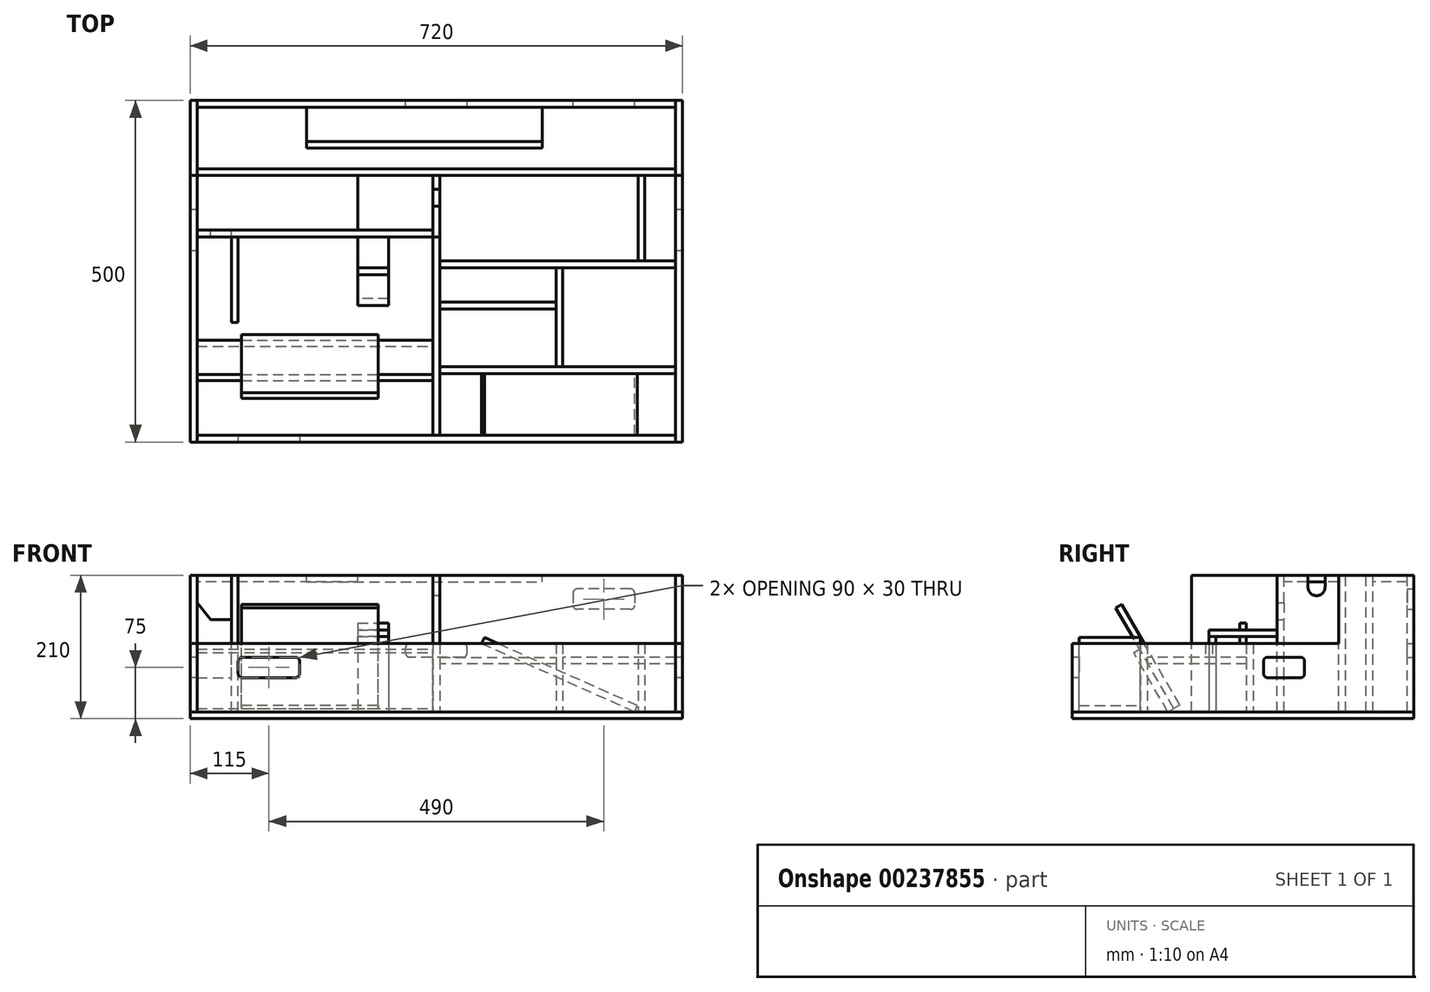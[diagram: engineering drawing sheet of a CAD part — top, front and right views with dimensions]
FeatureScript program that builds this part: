
annotation { "Feature Type Name" : "Feature", "Feature Type Description" : "" }
export const myFeature = defineFeature(function(context is Context, id is Id, definition is map)
    precondition{}
    {
        {
            var Q0;
            Q0=qCreatedBy(makeId("Top.planeOp"),FACE);
            var sketch = newSketch(context, id + "F0", { "sketchPlane" : qUnion([Q0])});
            skLineSegment(sketch, "E0.bottom", {"start": v(360, 250) * mm, "end": v(-360, 250) * mm});
            skLineSegment(sketch, "E0.top", {"start": v(360, -250) * mm, "end": v(-360, -250) * mm});
            skLineSegment(sketch, "E0.left", {"start": v(360, 250) * mm, "end": v(360, -250) * mm});
            skLineSegment(sketch, "E0.right", {"start": v(-360, 250) * mm, "end": v(-360, -250) * mm});
            skPoint(sketch, "E0.middle", {"position": v(0, 0) * mm});
            skSolve(sketch);
        }
        {
            var Q0;
            Q0=makeQuery(id+"F0.imprint","IMPRINT",FACE,{"disambiguationData":[TD([[makeQuery(id+"F0.imprint","IMPRINT",EDGE,{"derivedFrom":sQuery(id+"F0.wireOp",EDGE,"E0.bottom")}),1.0]])]});
            extrude(context, id + "F1", {"entities" : qUnion([Q0]), "depth" : 10 * mm});
        }
        {
            var Q0;
            Q0=makeQuery(id+"F1.opExtrude","SWEPT_FACE",FACE,{"disambiguationData":[OSD([sQuery(id+"F0.wireOp",EDGE,"E0.right")])]});
            var sketch = newSketch(context, id + "F2", { "sketchPlane" : qUnion([Q0])});
            skLineSegment(sketch, "E1.bottom", {"start": v(-250, 10) * mm, "end": v(250, 10) * mm});
            skLineSegment(sketch, "E1.top", {"start": v(-140, 110) * mm, "end": v(250, 110) * mm});
            skLineSegment(sketch, "E1.left", {"start": v(-250, 10) * mm, "end": v(-250, 110) * mm});
            skLineSegment(sketch, "E1.right", {"start": v(250, 10) * mm, "end": v(250, 110) * mm});
            skLineSegment(sketch, "E2.top", {"start": v(-250, 210) * mm, "end": v(-140, 210) * mm});
            skLineSegment(sketch, "E2.left", {"start": v(-250, 110) * mm, "end": v(-250, 210) * mm});
            skLineSegment(sketch, "E2.right", {"start": v(-140, 110) * mm, "end": v(-140, 210) * mm});
            skLineSegment(sketch, "E3.bottom", {"start": v(-250, 10) * mm, "end": v(-90, 10) * mm, "construction": true});
            skLineSegment(sketch, "E3.top", {"start": v(-250, 60) * mm, "end": v(-90, 60) * mm, "construction": true});
            skLineSegment(sketch, "E3.left", {"start": v(-250, 10) * mm, "end": v(-250, 60) * mm, "construction": true});
            skLineSegment(sketch, "E3.right", {"start": v(-90, 10) * mm, "end": v(-90, 60) * mm, "construction": true});
            skLineSegment(sketch, "E4.bottom", {"start": v(-84, 60) * mm, "end": v(-36, 60) * mm});
            skLineSegment(sketch, "E4.top", {"start": v(-84, 90) * mm, "end": v(-36, 90) * mm});
            skLineSegment(sketch, "E4.left", {"start": v(-90, 66) * mm, "end": v(-90, 84) * mm});
            skLineSegment(sketch, "E4.right", {"start": v(-30, 66) * mm, "end": v(-30, 84) * mm});
            skPoint(sketch, "E5.visualSharp", {"position": v(-90, 90) * mm});
            skArc(sketch, "E5.filletArc", {"start": v(-84, 90) * mm, "mid": v(-88.24, 88.24) * mm, "end": v(-90, 84) * mm});
            skPoint(sketch, "E6.visualSharp", {"position": v(-30, 90) * mm});
            skArc(sketch, "E6.filletArc", {"start": v(-30, 84) * mm, "mid": v(-31.76, 88.24) * mm, "end": v(-36, 90) * mm});
            skPoint(sketch, "E7.visualSharp", {"position": v(-30, 60) * mm});
            skArc(sketch, "E7.filletArc", {"start": v(-36, 60) * mm, "mid": v(-31.76, 61.76) * mm, "end": v(-30, 66) * mm});
            skPoint(sketch, "E8.visualSharp", {"position": v(-90, 60) * mm});
            skArc(sketch, "E8.filletArc", {"start": v(-90, 66) * mm, "mid": v(-88.24, 61.76) * mm, "end": v(-84, 60) * mm});
            skSolve(sketch);
        }
        {
            var Q0;
            Q0=makeQuery(id+"F2.imprint","IMPRINT",FACE,{"disambiguationData":[TD([[makeQuery(id+"F2.imprint","IMPRINT",EDGE,{"derivedFrom":sQuery(id+"F2.wireOp",EDGE,"E1.bottom")}),1.0]])]});
            extrude(context, id + "F3", {"entities" : qUnion([Q0]), "oppositeDirection" : true, "depth" : 10 * mm});
        }
        {
            var Q0;
            Q0=makeQuery(id+"F1.opExtrude","SWEPT_FACE",FACE,{"disambiguationData":[OSD([sQuery(id+"F0.wireOp",EDGE,"E0.left")])]});
            var sketch = newSketch(context, id + "F4", { "sketchPlane" : qUnion([Q0])});
            skLineSegment(sketch, "E9.0.0", {"start": v(250, 10) * mm, "end": v(250, 210) * mm});
            skLineSegment(sketch, "E9.0.1", {"start": v(250, 210) * mm, "end": v(140, 210) * mm});
            skLineSegment(sketch, "E9.0.2", {"start": v(140, 210) * mm, "end": v(140, 110) * mm});
            skLineSegment(sketch, "E9.0.3", {"start": v(140, 110) * mm, "end": v(-250, 110) * mm});
            skLineSegment(sketch, "E9.0.4", {"start": v(-250, 110) * mm, "end": v(-250, 10) * mm});
            skLineSegment(sketch, "E9.0.5", {"start": v(-250, 10) * mm, "end": v(250, 10) * mm});
            skLineSegment(sketch, "E10.0", {"start": v(84, 60) * mm, "end": v(36, 60) * mm});
            skLineSegment(sketch, "E11.0", {"start": v(84, 90) * mm, "end": v(36, 90) * mm});
            skArc(sketch, "E12.0", {"start": v(30, 84) * mm, "mid": v(31.76, 88.24) * mm, "end": v(36, 90) * mm});
            skLineSegment(sketch, "E13.0", {"start": v(30, 66) * mm, "end": v(30, 84) * mm});
            skArc(sketch, "E14.0", {"start": v(36, 60) * mm, "mid": v(31.76, 61.76) * mm, "end": v(30, 66) * mm});
            skArc(sketch, "E15.0", {"start": v(90, 66) * mm, "mid": v(88.24, 61.76) * mm, "end": v(84, 60) * mm});
            skLineSegment(sketch, "E16.0", {"start": v(90, 66) * mm, "end": v(90, 84) * mm});
            skArc(sketch, "E17.0", {"start": v(84, 90) * mm, "mid": v(88.24, 88.24) * mm, "end": v(90, 84) * mm});
            skSolve(sketch);
        }
        {
            var Q0;
            Q0 = qSketchRegion(id + "F4", true);
            extrude(context, id + "F5", {"entities" : qUnion([Q0]), "oppositeDirection" : true, "depth" : 10 * mm});
        }
        {
            var Q0;
            Q0=makeQuery(id+"F1.opExtrude","SWEPT_FACE",FACE,{"disambiguationData":[OSD([sQuery(id+"F0.wireOp",EDGE,"E0.top")])]});
            var sketch = newSketch(context, id + "F6", { "sketchPlane" : qUnion([Q0])});
            skLineSegment(sketch, "E18.0", {"start": v(-350, 10) * mm, "end": v(-350, 110) * mm});
            skLineSegment(sketch, "E19.0", {"start": v(350, 110) * mm, "end": v(350, 10) * mm});
            skLineSegment(sketch, "E20", {"start": v(-350, 110) * mm, "end": v(350, 110) * mm});
            skLineSegment(sketch, "E21", {"start": v(-350, 10) * mm, "end": v(350, 10) * mm});
            skLineSegment(sketch, "E22.bottom", {"start": v(-350, 110) * mm, "end": v(-290, 110) * mm, "construction": true});
            skLineSegment(sketch, "E22.top", {"start": v(-350, 90) * mm, "end": v(-290, 90) * mm, "construction": true});
            skLineSegment(sketch, "E22.left", {"start": v(-350, 110) * mm, "end": v(-350, 90) * mm, "construction": true});
            skLineSegment(sketch, "E22.right", {"start": v(-290, 110) * mm, "end": v(-290, 90) * mm, "construction": true});
            skLineSegment(sketch, "E23.bottom", {"start": v(-284, 90) * mm, "end": v(-206, 90) * mm});
            skLineSegment(sketch, "E23.top", {"start": v(-284, 60) * mm, "end": v(-206, 60) * mm});
            skLineSegment(sketch, "E23.left", {"start": v(-290, 84) * mm, "end": v(-290, 66) * mm});
            skLineSegment(sketch, "E23.right", {"start": v(-200, 84) * mm, "end": v(-200, 66) * mm});
            skPoint(sketch, "E24.visualSharp", {"position": v(-200, 90) * mm});
            skArc(sketch, "E24.filletArc", {"start": v(-200, 84) * mm, "mid": v(-201.76, 88.24) * mm, "end": v(-206, 90) * mm});
            skPoint(sketch, "E25.visualSharp", {"position": v(-200, 60) * mm});
            skArc(sketch, "E25.filletArc", {"start": v(-206, 60) * mm, "mid": v(-201.76, 61.76) * mm, "end": v(-200, 66) * mm});
            skPoint(sketch, "E26.visualSharp", {"position": v(-290, 60) * mm});
            skArc(sketch, "E26.filletArc", {"start": v(-290, 66) * mm, "mid": v(-288.24, 61.76) * mm, "end": v(-284, 60) * mm});
            skPoint(sketch, "E27.visualSharp", {"position": v(-290, 90) * mm});
            skArc(sketch, "E27.filletArc", {"start": v(-284, 90) * mm, "mid": v(-288.24, 88.24) * mm, "end": v(-290, 84) * mm});
            skSolve(sketch);
        }
        {
            var Q0;
            Q0 = qSketchRegion(id + "F6", true);
            extrude(context, id + "F7", {"entities" : qUnion([Q0]), "oppositeDirection" : true, "depth" : 10 * mm});
        }
        {
            var Q0;
            Q0=makeQuery(id+"F1.opExtrude","SWEPT_FACE",FACE,{"disambiguationData":[OSD([sQuery(id+"F0.wireOp",EDGE,"E0.bottom")])]});
            var sketch = newSketch(context, id + "F8", { "sketchPlane" : qUnion([Q0])});
            skLineSegment(sketch, "E28.0", {"start": v(-350, 10) * mm, "end": v(-350, 210) * mm});
            skLineSegment(sketch, "E29.0", {"start": v(350, 10) * mm, "end": v(350, 210) * mm});
            skLineSegment(sketch, "E30", {"start": v(-350, 10) * mm, "end": v(350, 10) * mm});
            skLineSegment(sketch, "E31", {"start": v(350, 210) * mm, "end": v(-350, 210) * mm});
            skLineSegment(sketch, "E32.bottom", {"start": v(-350, 210) * mm, "end": v(-290, 210) * mm, "construction": true});
            skLineSegment(sketch, "E32.top", {"start": v(-350, 190) * mm, "end": v(-290, 190) * mm, "construction": true});
            skLineSegment(sketch, "E32.left", {"start": v(-350, 210) * mm, "end": v(-350, 190) * mm, "construction": true});
            skLineSegment(sketch, "E32.right", {"start": v(-290, 210) * mm, "end": v(-290, 190) * mm, "construction": true});
            skLineSegment(sketch, "E33.bottom", {"start": v(-350, 10) * mm, "end": v(-45, 10) * mm, "construction": true});
            skLineSegment(sketch, "E33.top", {"start": v(-350, 90) * mm, "end": v(-45, 90) * mm, "construction": true});
            skLineSegment(sketch, "E33.left", {"start": v(-350, 10) * mm, "end": v(-350, 90) * mm, "construction": true});
            skLineSegment(sketch, "E33.right", {"start": v(-45, 10) * mm, "end": v(-45, 90) * mm, "construction": true});
            skLineSegment(sketch, "E34.bottom", {"start": v(-39, 90) * mm, "end": v(39, 90) * mm});
            skLineSegment(sketch, "E34.top", {"start": v(-39, 110) * mm, "end": v(39, 110) * mm});
            skLineSegment(sketch, "E34.left", {"start": v(-45, 96) * mm, "end": v(-45, 104) * mm});
            skLineSegment(sketch, "E34.right", {"start": v(45, 96) * mm, "end": v(45, 104) * mm});
            skLineSegment(sketch, "E35.bottom", {"start": v(-284, 190) * mm, "end": v(-206, 190) * mm});
            skLineSegment(sketch, "E35.top", {"start": v(-284, 160) * mm, "end": v(-206, 160) * mm});
            skLineSegment(sketch, "E35.left", {"start": v(-290, 184) * mm, "end": v(-290, 166) * mm});
            skLineSegment(sketch, "E35.right", {"start": v(-200, 184) * mm, "end": v(-200, 166) * mm});
            skPoint(sketch, "E36.visualSharp", {"position": v(-290, 190) * mm});
            skArc(sketch, "E36.filletArc", {"start": v(-284, 190) * mm, "mid": v(-288.24, 188.24) * mm, "end": v(-290, 184) * mm});
            skPoint(sketch, "E37.visualSharp", {"position": v(-290, 160) * mm});
            skArc(sketch, "E37.filletArc", {"start": v(-290, 166) * mm, "mid": v(-288.24, 161.76) * mm, "end": v(-284, 160) * mm});
            skPoint(sketch, "E38.visualSharp", {"position": v(-200, 190) * mm});
            skArc(sketch, "E38.filletArc", {"start": v(-200, 184) * mm, "mid": v(-201.76, 188.24) * mm, "end": v(-206, 190) * mm});
            skPoint(sketch, "E39.visualSharp", {"position": v(-200, 160) * mm});
            skArc(sketch, "E39.filletArc", {"start": v(-206, 160) * mm, "mid": v(-201.76, 161.76) * mm, "end": v(-200, 166) * mm});
            skPoint(sketch, "E40.visualSharp", {"position": v(-45, 110) * mm});
            skArc(sketch, "E40.filletArc", {"start": v(-39, 110) * mm, "mid": v(-43.24, 108.24) * mm, "end": v(-45, 104) * mm});
            skPoint(sketch, "E41.visualSharp", {"position": v(45, 110) * mm});
            skArc(sketch, "E41.filletArc", {"start": v(45, 104) * mm, "mid": v(43.24, 108.24) * mm, "end": v(39, 110) * mm});
            skPoint(sketch, "E42.visualSharp", {"position": v(45, 90) * mm});
            skArc(sketch, "E42.filletArc", {"start": v(39, 90) * mm, "mid": v(43.24, 91.76) * mm, "end": v(45, 96) * mm});
            skPoint(sketch, "E43.visualSharp", {"position": v(-45, 90) * mm});
            skArc(sketch, "E43.filletArc", {"start": v(-45, 96) * mm, "mid": v(-43.24, 91.76) * mm, "end": v(-39, 90) * mm});
            skSolve(sketch);
        }
        {
            var Q0;
            Q0=makeQuery(id+"F8.imprint","IMPRINT",FACE,{"disambiguationData":[TD([[makeQuery(id+"F8.imprint","IMPRINT",EDGE,{"derivedFrom":sQuery(id+"F8.wireOp",EDGE,"E28.0")}),-1.0]])]});
            extrude(context, id + "F9", {"entities" : qUnion([Q0]), "oppositeDirection" : true, "depth" : 10 * mm});
        }
        {
            var Q0;
            Q0=makeQuery(id+"F5.opExtrude","SWEPT_FACE",FACE,{"disambiguationData":[OSD([sQuery(id+"F4.wireOp",EDGE,"E9.0.2")])]});
            var sketch = newSketch(context, id + "F10", { "sketchPlane" : qUnion([Q0])});
            skLineSegment(sketch, "E44.0.0", {"start": v(-350, 10) * mm, "end": v(350, 10) * mm});
            skLineSegment(sketch, "E44.0.1", {"start": v(350, 10) * mm, "end": v(350, 210) * mm});
            skLineSegment(sketch, "E44.0.2", {"start": v(350, 210) * mm, "end": v(-350, 210) * mm});
            skLineSegment(sketch, "E44.0.3", {"start": v(-350, 210) * mm, "end": v(-350, 10) * mm});
            skSolve(sketch);
        }
        {
            var Q0;
            {var subQ4=sQuery(id+"F10.wireOp",EDGE,"E44.0.0");Q0=makeQuery(id+"F10.imprint","IMPRINT",FACE,{"disambiguationData":[TD([[makeQuery(id+"F10.imprint","IMPRINT",EDGE,{"derivedFrom":subQ4}),1.0]])]});}
            extrude(context, id + "F11", {"entities" : qUnion([Q0]), "oppositeDirection" : true, "depth" : 10 * mm});
        }
        {
            var Q0;
            Q0=makeQuery(id+"F9.opExtrude","SWEPT_FACE",FACE,{"disambiguationData":[OSD([sQuery(id+"F8.wireOp",EDGE,"E31")])]});
            var sketch = newSketch(context, id + "F12", { "sketchPlane" : qUnion([Q0])});
            skLineSegment(sketch, "E45", {"start": v(-350, 240) * mm, "end": v(-190, 240) * mm, "construction": true});
            skLineSegment(sketch, "E46.bottom", {"start": v(-190, 240) * mm, "end": v(155, 240) * mm});
            skLineSegment(sketch, "E46.top", {"start": v(-190, 190) * mm, "end": v(155, 190) * mm});
            skLineSegment(sketch, "E46.left", {"start": v(-190, 240) * mm, "end": v(-190, 190) * mm});
            skLineSegment(sketch, "E46.right", {"start": v(155, 240) * mm, "end": v(155, 190) * mm});
            skSolve(sketch);
        }
        {
            var Q0;
            Q0=makeQuery(id+"F12.imprint","IMPRINT",FACE,{"disambiguationData":[TD([[makeQuery(id+"F12.imprint","IMPRINT",EDGE,{"derivedFrom":sQuery(id+"F12.wireOp",EDGE,"E46.bottom")}),-1.0]])]});
            extrude(context, id + "F13", {"entities" : qUnion([Q0]), "oppositeDirection" : true, "depth" : 10 * mm});
        }
        {
            var Q0;
            Q0=makeQuery(id+"F13.opExtrude","SWEPT_FACE",FACE,{"disambiguationData":[OSD([sQuery(id+"F12.wireOp",EDGE,"E46.top")])]});
            var sketch = newSketch(context, id + "F14", { "sketchPlane" : qUnion([Q0])});
            skLineSegment(sketch, "E47.0", {"start": v(155, 210) * mm, "end": v(-190, 210) * mm});
            skLineSegment(sketch, "E48.0", {"start": v(155, 10) * mm, "end": v(-190, 10) * mm});
            skLineSegment(sketch, "E49", {"start": v(-190, 210) * mm, "end": v(-190, 10) * mm});
            skPoint(sketch, "E49.endSnap0", {"position": v(-190, 205) * mm});
            skLineSegment(sketch, "E50", {"start": v(155, 210) * mm, "end": v(155, 10) * mm});
            skPoint(sketch, "E51.orphan", {"position": v(-350, 210) * mm});
            skPoint(sketch, "E52.orphan", {"position": v(-360, 10) * mm});
            skPoint(sketch, "E53.orphan", {"position": v(360, 10) * mm});
            skPoint(sketch, "E54.orphan", {"position": v(350, 210) * mm});
            skSolve(sketch);
        }
        {
            var Q0;
            Q0 = qSketchRegion(id + "F14", true);
            extrude(context, id + "F15", {"entities" : qUnion([Q0]), "depth" : 10 * mm});
        }
        {
            var Q0;
            Q0=makeQuery(id+"F11.opExtrude","SWEPT_FACE",FACE,{"disambiguationData":[OSD([sQuery(id+"F10.wireOp",EDGE,"E44.0.2")])]});
            var sketch = newSketch(context, id + "F16", { "sketchPlane" : qUnion([Q0])});
            skLineSegment(sketch, "E55.bottom", {"start": v(-350, 140) * mm, "end": v(-115, 140) * mm});
            skLineSegment(sketch, "E55.top", {"start": v(-350, 60) * mm, "end": v(-115, 60) * mm});
            skLineSegment(sketch, "E55.left", {"start": v(-350, 140) * mm, "end": v(-350, 60) * mm});
            skLineSegment(sketch, "E55.right", {"start": v(-115, 140) * mm, "end": v(-115, 60) * mm});
            skSolve(sketch);
        }
        {
            var Q0;
            Q0 = qSketchRegion(id + "F16", true);
            extrude(context, id + "F17", {"entities" : qUnion([Q0]), "oppositeDirection" : true, "depth" : 10 * mm});
        }
        {
            var Q0;
            Q0=makeQuery(id+"F17.opExtrude","SWEPT_FACE",FACE,{"disambiguationData":[OSD([sQuery(id+"F16.wireOp",EDGE,"E55.top")])]});
            var sketch = newSketch(context, id + "F18", { "sketchPlane" : qUnion([Q0])});
            skLineSegment(sketch, "E56", {"start": v(-350, 210) * mm, "end": v(-5, 210) * mm});
            skLineSegment(sketch, "E57", {"start": v(-5, 210) * mm, "end": v(-5, 10) * mm});
            skLineSegment(sketch, "E58", {"start": v(-5, 10) * mm, "end": v(-350, 10) * mm});
            skLineSegment(sketch, "E59", {"start": v(-350, 10) * mm, "end": v(-350, 60) * mm});
            skLineSegment(sketch, "E60", {"start": v(-350, 60) * mm, "end": v(-300, 60) * mm});
            skLineSegment(sketch, "E61", {"start": v(-300, 60) * mm, "end": v(-300, 145) * mm});
            skLineSegment(sketch, "E62", {"start": v(-300, 145) * mm, "end": v(-330, 145) * mm});
            skLineSegment(sketch, "E63", {"start": v(-350, 210) * mm, "end": v(-350, 170) * mm});
            skLineSegment(sketch, "E64", {"start": v(-350, 170) * mm, "end": v(-330, 145) * mm});
            skSolve(sketch);
        }
        {
            var Q0;
            Q0 = qSketchRegion(id + "F18", true);
            extrude(context, id + "F19", {"entities" : qUnion([Q0]), "depth" : 10 * mm});
        }
        {
            var Q0;
            Q0=makeQuery(id+"F19.opExtrude","SWEPT_FACE",FACE,{"disambiguationData":[OSD([sQuery(id+"F18.wireOp",EDGE,"E57")])]});
            var sketch = newSketch(context, id + "F20", { "sketchPlane" : qUnion([Q0])});
            skLineSegment(sketch, "E65.0", {"start": v(50, 210) * mm, "end": v(50, 110) * mm});
            skLineSegment(sketch, "E66.0", {"start": v(140, 210) * mm, "end": v(140, 110) * mm});
            skLineSegment(sketch, "E66.1", {"start": v(140, 210) * mm, "end": v(140, 10) * mm});
            skLineSegment(sketch, "E67.0", {"start": v(140, 210) * mm, "end": v(120, 210) * mm});
            skLineSegment(sketch, "E67.1", {"start": v(50, 210) * mm, "end": v(60, 210) * mm});
            skLineSegment(sketch, "E68", {"start": v(50, 10) * mm, "end": v(140, 10) * mm});
            skLineSegment(sketch, "E69", {"start": v(140, 210) * mm, "end": v(120, 210) * mm, "construction": true});
            skLineSegment(sketch, "E70", {"start": v(107.5, 210) * mm, "end": v(107.5, 192.5) * mm, "construction": true});
            skArc(sketch, "E71", {"start": v(95, 192.5) * mm, "mid": v(107.5, 180) * mm, "end": v(120, 192.5) * mm});
            skLineSegment(sketch, "E72", {"start": v(120, 210) * mm, "end": v(120, 192.5) * mm});
            skLineSegment(sketch, "E73", {"start": v(95, 192.5) * mm, "end": v(95, 210) * mm});
            skLineSegment(sketch, "E74.trimOffspring", {"start": v(95, 210) * mm, "end": v(60, 210) * mm});
            skLineSegment(sketch, "E75.0", {"start": v(-240, 110) * mm, "end": v(-240, 10) * mm});
            skLineSegment(sketch, "E76", {"start": v(50, 10) * mm, "end": v(-240, 10) * mm});
            skLineSegment(sketch, "E77", {"start": v(-240, 110) * mm, "end": v(50, 110) * mm});
            skSolve(sketch);
        }
        {
            var Q0;
            Q0 = qSketchRegion(id + "F20", true);
            extrude(context, id + "F21", {"entities" : qUnion([Q0]), "depth" : 10 * mm});
        }
        {
            var Q0;
            Q0=makeQuery(id+"F21.opExtrude","CAP_FACE",FACE,{"disambiguationData":[OSD([sQuery(id+"F20.wireOp",EDGE,"E65.0"),sQuery(id+"F20.wireOp",EDGE,"E66.1"),sQuery(id+"F20.wireOp",EDGE,"E67.0"),sQuery(id+"F20.wireOp",EDGE,"E67.1"),sQuery(id+"F20.wireOp",EDGE,"E68"),sQuery(id+"F20.wireOp",EDGE,"E71"),sQuery(id+"F20.wireOp",EDGE,"E72"),sQuery(id+"F20.wireOp",EDGE,"E73"),sQuery(id+"F20.wireOp",EDGE,"E74.trimOffspring"),sQuery(id+"F20.wireOp",EDGE,"E75.0"),sQuery(id+"F20.wireOp",EDGE,"E76"),sQuery(id+"F20.wireOp",EDGE,"E77")])],"isStart":false});
            var sketch = newSketch(context, id + "F22", { "sketchPlane" : qUnion([Q0])});
            skLineSegment(sketch, "E78", {"start": v(140, 110) * mm, "end": v(15, 110) * mm, "construction": true});
            skLineSegment(sketch, "E79", {"start": v(15, 110) * mm, "end": v(-140, 110) * mm, "construction": true});
            skLineSegment(sketch, "E80.bottom", {"start": v(15, 110) * mm, "end": v(5, 110) * mm});
            skLineSegment(sketch, "E80.top", {"start": v(15, 10) * mm, "end": v(5, 10) * mm});
            skLineSegment(sketch, "E80.left", {"start": v(15, 110) * mm, "end": v(15, 10) * mm});
            skLineSegment(sketch, "E80.right", {"start": v(5, 110) * mm, "end": v(5, 10) * mm});
            skLineSegment(sketch, "E81.bottom", {"start": v(-140, 110) * mm, "end": v(-150, 110) * mm});
            skLineSegment(sketch, "E81.top", {"start": v(-140, 10) * mm, "end": v(-150, 10) * mm});
            skLineSegment(sketch, "E81.left", {"start": v(-140, 110) * mm, "end": v(-140, 10) * mm});
            skLineSegment(sketch, "E81.right", {"start": v(-150, 110) * mm, "end": v(-150, 10) * mm});
            skSolve(sketch);
        }
        {
            var Q0;
            Q0 = qSketchRegion(id + "F22", true);
            extrude(context, id + "F23", {"entities" : qUnion([Q0]), "endBound" : BoundingType.UP_TO_NEXT, "depth" : 25 * mm});
        }
        {
            var Q0;
            Q0=makeQuery(id+"F11.opExtrude","CAP_FACE",FACE,{"disambiguationData":[OSD([sQuery(id+"F10.wireOp",EDGE,"E44.0.0"),sQuery(id+"F10.wireOp",EDGE,"E44.0.1"),sQuery(id+"F10.wireOp",EDGE,"E44.0.2"),sQuery(id+"F10.wireOp",EDGE,"E44.0.3")])],"isStart":true});
            var sketch = newSketch(context, id + "F24", { "sketchPlane" : qUnion([Q0])});
            skLineSegment(sketch, "E82", {"start": v(350, 10) * mm, "end": v(305, 10) * mm, "construction": true});
            skLineSegment(sketch, "E83.bottom", {"start": v(305, 10) * mm, "end": v(295, 10) * mm});
            skLineSegment(sketch, "E83.top", {"start": v(305, 110) * mm, "end": v(295, 110) * mm});
            skLineSegment(sketch, "E83.left", {"start": v(305, 10) * mm, "end": v(305, 110) * mm});
            skLineSegment(sketch, "E83.right", {"start": v(295, 10) * mm, "end": v(295, 110) * mm});
            skSolve(sketch);
        }
        {
            var Q0;
            Q0 = qSketchRegion(id + "F24", true);
            extrude(context, id + "F25", {"entities" : qUnion([Q0]), "endBound" : BoundingType.UP_TO_NEXT, "depth" : 25 * mm});
        }
        {
            var Q0;
            Q0=makeQuery(id+"F21.opExtrude","CAP_FACE",FACE,{"disambiguationData":[OSD([sQuery(id+"F20.wireOp",EDGE,"E65.0"),sQuery(id+"F20.wireOp",EDGE,"E66.1"),sQuery(id+"F20.wireOp",EDGE,"E67.0"),sQuery(id+"F20.wireOp",EDGE,"E67.1"),sQuery(id+"F20.wireOp",EDGE,"E68"),sQuery(id+"F20.wireOp",EDGE,"E71"),sQuery(id+"F20.wireOp",EDGE,"E72"),sQuery(id+"F20.wireOp",EDGE,"E73"),sQuery(id+"F20.wireOp",EDGE,"E74.trimOffspring"),sQuery(id+"F20.wireOp",EDGE,"E75.0"),sQuery(id+"F20.wireOp",EDGE,"E76"),sQuery(id+"F20.wireOp",EDGE,"E77")])],"isStart":false});
            var sketch = newSketch(context, id + "F26", { "sketchPlane" : qUnion([Q0])});
            skLineSegment(sketch, "E84.0", {"start": v(5, 90) * mm, "end": v(5, 80) * mm});
            skPoint(sketch, "E85.orphan", {"position": v(5, 10) * mm});
            skLineSegment(sketch, "E86.bottom", {"start": v(5, 80) * mm, "end": v(-140, 80) * mm});
            skLineSegment(sketch, "E86.top", {"start": v(5, 90) * mm, "end": v(-140, 90) * mm});
            skLineSegment(sketch, "E86.left", {"start": v(5, 80) * mm, "end": v(5, 90) * mm});
            skLineSegment(sketch, "E86.right", {"start": v(-140, 80) * mm, "end": v(-140, 90) * mm});
            skPoint(sketch, "E87.orphan", {"position": v(5, 110) * mm});
            skSolve(sketch);
        }
        {
            var Q0;
            Q0 = qSketchRegion(id + "F26", true);
            extrude(context, id + "F27", {"entities" : qUnion([Q0]), "depth" : 170 * mm});
        }
        {
            var Q0;
            Q0=makeQuery(id+"F27.opExtrude","CAP_FACE",FACE,{"disambiguationData":[OSD([sQuery(id+"F26.wireOp",EDGE,"E86.bottom"),sQuery(id+"F26.wireOp",EDGE,"E86.top"),sQuery(id+"F26.wireOp",EDGE,"E86.left"),sQuery(id+"F26.wireOp",EDGE,"E86.right")])],"isStart":false});
            var sketch = newSketch(context, id + "F28", { "sketchPlane" : qUnion([Q0])});
            skLineSegment(sketch, "E88.0", {"start": v(-140, 110) * mm, "end": v(-140, 10) * mm});
            skLineSegment(sketch, "E89.0", {"start": v(5, 110) * mm, "end": v(5, 10) * mm});
            skLineSegment(sketch, "E90", {"start": v(-140, 110) * mm, "end": v(5, 110) * mm});
            skLineSegment(sketch, "E91", {"start": v(5, 10) * mm, "end": v(-140, 10) * mm});
            skSolve(sketch);
        }
        {
            var Q0;
            Q0 = qSketchRegion(id + "F28", true);
            extrude(context, id + "F29", {"entities" : qUnion([Q0]), "depth" : 10 * mm});
        }
        {
            var Q0;
            Q0=makeQuery(id+"F27.opExtrude","SWEPT_FACE",FACE,{"disambiguationData":[OSD([sQuery(id+"F26.wireOp",EDGE,"E86.top")])]});
            var sketch = newSketch(context, id + "F30", { "sketchPlane" : qUnion([Q0])});
            skLineSegment(sketch, "E92", {"start": v(5, -140) * mm, "end": v(5, -55) * mm, "construction": true});
            skLineSegment(sketch, "E93.bottom", {"start": v(5, -55) * mm, "end": v(175, -55) * mm});
            skLineSegment(sketch, "E93.top", {"start": v(5, -45) * mm, "end": v(175, -45) * mm});
            skLineSegment(sketch, "E93.left", {"start": v(5, -55) * mm, "end": v(5, -45) * mm});
            skLineSegment(sketch, "E93.right", {"start": v(175, -55) * mm, "end": v(175, -45) * mm});
            skSolve(sketch);
        }
        {
            var Q0;
            Q0 = qSketchRegion(id + "F30", true);
            var Q1;
            Q1=makeQuery(id+"F21.opExtrude","SWEPT_FACE",FACE,{"disambiguationData":[OSD([sQuery(id+"F20.wireOp",EDGE,"E77")])]});
            extrude(context, id + "F31", {"entities" : qUnion([Q0]), "endBound" : BoundingType.UP_TO_SURFACE, "endBoundEntityFace" : qUnion([Q1]), "depth" : 25 * mm});
        }
        {
            var Q0;
            Q0=makeQuery(id+"F29.opExtrude","CAP_FACE",FACE,{"disambiguationData":[OSD([sQuery(id+"F28.wireOp",EDGE,"E88.0"),sQuery(id+"F28.wireOp",EDGE,"E89.0"),sQuery(id+"F28.wireOp",EDGE,"E90"),sQuery(id+"F28.wireOp",EDGE,"E91")])],"isStart":false});
            var sketch = newSketch(context, id + "F32", { "sketchPlane" : qUnion([Q0])});
            skLineSegment(sketch, "E94.0", {"start": v(5, 90) * mm, "end": v(-140, 90) * mm});
            skLineSegment(sketch, "E95.0", {"start": v(5, 80) * mm, "end": v(-140, 80) * mm});
            skLineSegment(sketch, "E96", {"start": v(-140, 90) * mm, "end": v(-140, 80) * mm});
            skLineSegment(sketch, "E97", {"start": v(5, 90) * mm, "end": v(5, 80) * mm});
            skSolve(sketch);
        }
        {
            var Q0;
            Q0 = qSketchRegion(id + "F32", true);
            extrude(context, id + "F33", {"entities" : qUnion([Q0]), "endBound" : BoundingType.UP_TO_NEXT, "depth" : 25 * mm});
        }
        {
            var Q0;
            Q0=makeQuery(id+"F19.opExtrude","CAP_FACE",FACE,{"disambiguationData":[OSD([sQuery(id+"F18.wireOp",EDGE,"E56"),sQuery(id+"F18.wireOp",EDGE,"E57"),sQuery(id+"F18.wireOp",EDGE,"E58"),sQuery(id+"F18.wireOp",EDGE,"E59"),sQuery(id+"F18.wireOp",EDGE,"E60"),sQuery(id+"F18.wireOp",EDGE,"E61"),sQuery(id+"F18.wireOp",EDGE,"E62"),sQuery(id+"F18.wireOp",EDGE,"E63"),sQuery(id+"F18.wireOp",EDGE,"E64")])],"isStart":false});
            var sketch = newSketch(context, id + "F34", { "sketchPlane" : qUnion([Q0])});
            skLineSegment(sketch, "E98.0", {"start": v(-300, 60) * mm, "end": v(-300, 145) * mm});
            skLineSegment(sketch, "E99", {"start": v(-300, 60) * mm, "end": v(-300, 10) * mm});
            skLineSegment(sketch, "E100", {"start": v(-300, 10) * mm, "end": v(-290, 10) * mm});
            skLineSegment(sketch, "E101", {"start": v(-290, 10) * mm, "end": v(-290, 210) * mm});
            skLineSegment(sketch, "E102", {"start": v(-290, 210) * mm, "end": v(-300, 210) * mm});
            skLineSegment(sketch, "E103", {"start": v(-300, 210) * mm, "end": v(-300, 145) * mm});
            skSolve(sketch);
        }
        {
            var Q0;
            Q0 = qSketchRegion(id + "F34", true);
            extrude(context, id + "F35", {"entities" : qUnion([Q0]), "depth" : 125 * mm});
        }
        {
            var Q0;
            Q0=makeQuery(id+"F19.opExtrude","CAP_FACE",FACE,{"disambiguationData":[OSD([sQuery(id+"F18.wireOp",EDGE,"E56"),sQuery(id+"F18.wireOp",EDGE,"E57"),sQuery(id+"F18.wireOp",EDGE,"E58"),sQuery(id+"F18.wireOp",EDGE,"E59"),sQuery(id+"F18.wireOp",EDGE,"E60"),sQuery(id+"F18.wireOp",EDGE,"E61"),sQuery(id+"F18.wireOp",EDGE,"E62"),sQuery(id+"F18.wireOp",EDGE,"E63"),sQuery(id+"F18.wireOp",EDGE,"E64")])],"isStart":false});
            var sketch = newSketch(context, id + "F36", { "sketchPlane" : qUnion([Q0])});
            skLineSegment(sketch, "E104.bottom", {"start": v(-5, 210) * mm, "end": v(-70, 210) * mm, "construction": true});
            skLineSegment(sketch, "E104.top", {"start": v(-5, 130) * mm, "end": v(-70, 130) * mm, "construction": true});
            skLineSegment(sketch, "E104.left", {"start": v(-5, 210) * mm, "end": v(-5, 130) * mm, "construction": true});
            skLineSegment(sketch, "E104.right", {"start": v(-70, 210) * mm, "end": v(-70, 130) * mm, "construction": true});
            skLineSegment(sketch, "E105.bottom", {"start": v(-70, 130) * mm, "end": v(-115, 130) * mm});
            skLineSegment(sketch, "E105.top", {"start": v(-70, 120) * mm, "end": v(-115, 120) * mm});
            skLineSegment(sketch, "E105.left", {"start": v(-70, 130) * mm, "end": v(-70, 120) * mm});
            skLineSegment(sketch, "E105.right", {"start": v(-115, 130) * mm, "end": v(-115, 120) * mm});
            skSolve(sketch);
        }
        {
            var Q0;
            Q0 = qSketchRegion(id + "F36", true);
            extrude(context, id + "F37", {"entities" : qUnion([Q0]), "depth" : 100 * mm});
        }
        {
            var Q0;
            Q0=makeQuery(id+"F37.opExtrude","CAP_FACE",FACE,{"disambiguationData":[OSD([sQuery(id+"F36.wireOp",EDGE,"E105.bottom"),sQuery(id+"F36.wireOp",EDGE,"E105.top"),sQuery(id+"F36.wireOp",EDGE,"E105.left"),sQuery(id+"F36.wireOp",EDGE,"E105.right")])],"isStart":false});
            var sketch = newSketch(context, id + "F38", { "sketchPlane" : qUnion([Q0])});
            skLineSegment(sketch, "E106.bottom", {"start": v(-115, 120) * mm, "end": v(-70, 120) * mm});
            skLineSegment(sketch, "E106.top", {"start": v(-115, 10) * mm, "end": v(-70, 10) * mm});
            skLineSegment(sketch, "E106.left", {"start": v(-115, 120) * mm, "end": v(-115, 10) * mm});
            skLineSegment(sketch, "E106.right", {"start": v(-70, 120) * mm, "end": v(-70, 10) * mm});
            skSolve(sketch);
        }
        {
            var Q0;
            Q0 = qSketchRegion(id + "F38", true);
            extrude(context, id + "F39", {"entities" : qUnion([Q0]), "oppositeDirection" : true, "depth" : 10 * mm});
        }
        {
            var Q0;
            Q0=makeQuery(id+"F37.opExtrude","SWEPT_FACE",FACE,{"disambiguationData":[OSD([sQuery(id+"F36.wireOp",EDGE,"E105.bottom")])]});
            var sketch = newSketch(context, id + "F40", { "sketchPlane" : qUnion([Q0])});
            skLineSegment(sketch, "E107", {"start": v(-115, -50) * mm, "end": v(-115, -5) * mm, "construction": true});
            skLineSegment(sketch, "E108.bottom", {"start": v(-115, -5) * mm, "end": v(-70, -5) * mm});
            skLineSegment(sketch, "E108.top", {"start": v(-115, 5) * mm, "end": v(-70, 5) * mm});
            skLineSegment(sketch, "E108.left", {"start": v(-115, -5) * mm, "end": v(-115, 5) * mm});
            skLineSegment(sketch, "E108.right", {"start": v(-70, -5) * mm, "end": v(-70, 5) * mm});
            skSolve(sketch);
        }
        {
            var Q0;
            Q0=makeQuery(id+"F40.imprint","IMPRINT",FACE,{"disambiguationData":[TD([[makeQuery(id+"F40.imprint","IMPRINT",EDGE,{"derivedFrom":sQuery(id+"F40.wireOp",EDGE,"E108.bottom")}),1.0]])]});
            extrude(context, id + "F41", {"entities" : qUnion([Q0]), "depth" : 10 * mm});
        }
        {
            var Q0;
            Q0=makeQuery(id+"F40.imprint","IMPRINT",FACE,{"disambiguationData":[TD([[makeQuery(id+"F40.imprint","IMPRINT",EDGE,{"derivedFrom":sQuery(id+"F40.wireOp",EDGE,"E108.bottom")}),1.0]])]});
            extrude(context, id + "F42", {"entities" : qUnion([Q0]), "oppositeDirection" : true, "depth" : 20 * mm, "hasSecondDirection" : true, "secondDirectionOppositeDirection" : true, "secondDirectionDepth" : 10 * mm});
        }
        {
            var Q0;
            Q0=makeQuery(id+"F23.opExtrude","SWEPT_FACE",FACE,{"disambiguationData":[OSD([sQuery(id+"F22.wireOp",EDGE,"E81.right")])]});
            var sketch = newSketch(context, id + "F43", { "sketchPlane" : qUnion([Q0])});
            skLineSegment(sketch, "E109", {"start": v(350, 10) * mm, "end": v(290, 10) * mm, "construction": true});
            skLineSegment(sketch, "E110", {"start": v(290, 10) * mm, "end": v(66.18, 109.65) * mm});
            skLineSegment(sketch, "E111", {"start": v(66.18, 109.65) * mm, "end": v(70.25, 118.79) * mm});
            skLineSegment(sketch, "E112", {"start": v(290, 10) * mm, "end": v(294.07, 19.14) * mm});
            skLineSegment(sketch, "E113", {"start": v(294.07, 19.14) * mm, "end": v(70.25, 118.79) * mm});
            skSolve(sketch);
        }
        {
            var Q0;
            Q0 = qSketchRegion(id + "F43", true);
            var Q1;
            Q1=makeQuery(id+"F7.opExtrude","CAP_FACE",FACE,{"disambiguationData":[OSD([sQuery(id+"F6.wireOp",EDGE,"E18.0"),sQuery(id+"F6.wireOp",EDGE,"E19.0"),sQuery(id+"F6.wireOp",EDGE,"E20"),sQuery(id+"F6.wireOp",EDGE,"E21"),sQuery(id+"F6.wireOp",EDGE,"E23.bottom"),sQuery(id+"F6.wireOp",EDGE,"E23.top"),sQuery(id+"F6.wireOp",EDGE,"E23.left"),sQuery(id+"F6.wireOp",EDGE,"E23.right"),sQuery(id+"F6.wireOp",EDGE,"E24.filletArc"),sQuery(id+"F6.wireOp",EDGE,"E25.filletArc"),sQuery(id+"F6.wireOp",EDGE,"E26.filletArc"),sQuery(id+"F6.wireOp",EDGE,"E27.filletArc")])],"isStart":false});
            extrude(context, id + "F44", {"entities" : qUnion([Q0]), "endBound" : BoundingType.UP_TO_SURFACE, "endBoundEntityFace" : qUnion([Q1]), "depth" : 25 * mm});
        }
        {
            var Q0;
            Q0=makeQuery(id+"F21.opExtrude","CAP_FACE",FACE,{"disambiguationData":[OSD([sQuery(id+"F20.wireOp",EDGE,"E65.0"),sQuery(id+"F20.wireOp",EDGE,"E66.1"),sQuery(id+"F20.wireOp",EDGE,"E67.0"),sQuery(id+"F20.wireOp",EDGE,"E67.1"),sQuery(id+"F20.wireOp",EDGE,"E68"),sQuery(id+"F20.wireOp",EDGE,"E71"),sQuery(id+"F20.wireOp",EDGE,"E72"),sQuery(id+"F20.wireOp",EDGE,"E73"),sQuery(id+"F20.wireOp",EDGE,"E74.trimOffspring"),sQuery(id+"F20.wireOp",EDGE,"E75.0"),sQuery(id+"F20.wireOp",EDGE,"E76"),sQuery(id+"F20.wireOp",EDGE,"E77")])],"isStart":true});
            var sketch = newSketch(context, id + "F45", { "sketchPlane" : qUnion([Q0])});
            skLineSegment(sketch, "E114", {"start": v(240, 10) * mm, "end": v(110, 10) * mm, "construction": true});
            skLineSegment(sketch, "E115", {"start": v(110, 10) * mm, "end": v(160, 96.6) * mm});
            skLineSegment(sketch, "E116", {"start": v(160, 96.6) * mm, "end": v(151.34, 101.6) * mm});
            skLineSegment(sketch, "E117", {"start": v(110, 10) * mm, "end": v(101.34, 15) * mm});
            skLineSegment(sketch, "E118", {"start": v(101.34, 15) * mm, "end": v(151.34, 101.6) * mm});
            skSolve(sketch);
        }
        {
            var Q0;
            Q0 = qSketchRegion(id + "F45", true);
            extrude(context, id + "F46", {"entities" : qUnion([Q0]), "endBound" : BoundingType.UP_TO_NEXT, "depth" : 25 * mm});
        }
        {
            var Q0;
            Q0=makeQuery(id+"F46.opExtrude","SWEPT_FACE",FACE,{"disambiguationData":[OSD([sQuery(id+"F45.wireOp",EDGE,"E118")])]});
            var sketch = newSketch(context, id + "F47", { "sketchPlane" : qUnion([Q0])});
            skLineSegment(sketch, "E119", {"start": v(350, 63.66) * mm, "end": v(285, 63.66) * mm, "construction": true});
            skLineSegment(sketch, "E120.bottom", {"start": v(285, 63.66) * mm, "end": v(85, 63.66) * mm});
            skLineSegment(sketch, "E120.top", {"start": v(285, 233.66) * mm, "end": v(85, 233.66) * mm});
            skLineSegment(sketch, "E120.left", {"start": v(285, 63.66) * mm, "end": v(285, 233.66) * mm});
            skLineSegment(sketch, "E120.right", {"start": v(85, 63.66) * mm, "end": v(85, 233.66) * mm});
            skSolve(sketch);
        }
        {
            var Q0;
            Q0 = qSketchRegion(id + "F47", true);
            extrude(context, id + "F48", {"entities" : qUnion([Q0]), "depth" : 10 * mm});
        }
        {
            var Q0;
            Q0=makeQuery(id+"F5.opExtrude","SWEPT_BODY",BODY,{"disambiguationData":[OSD([sQuery(id+"F4.wireOp",EDGE,"E9.0.0"),sQuery(id+"F4.wireOp",EDGE,"E9.0.1"),sQuery(id+"F4.wireOp",EDGE,"E9.0.2"),sQuery(id+"F4.wireOp",EDGE,"E9.0.3"),sQuery(id+"F4.wireOp",EDGE,"E9.0.4"),sQuery(id+"F4.wireOp",EDGE,"E9.0.5"),sQuery(id+"F4.wireOp",EDGE,"E10.0"),sQuery(id+"F4.wireOp",EDGE,"E11.0"),sQuery(id+"F4.wireOp",EDGE,"E12.0"),sQuery(id+"F4.wireOp",EDGE,"E13.0"),sQuery(id+"F4.wireOp",EDGE,"E14.0"),sQuery(id+"F4.wireOp",EDGE,"E15.0"),sQuery(id+"F4.wireOp",EDGE,"E16.0"),sQuery(id+"F4.wireOp",EDGE,"E17.0")])]});
            deleteBodies(context, id + "F49", {"entities" : qUnion([Q0])});
        }
        {
            var Q0;
            Q0=makeQuery(id+"F3.opExtrude","SWEPT_BODY",BODY,{"disambiguationData":[OSD([sQuery(id+"F2.wireOp",EDGE,"E1.bottom"),sQuery(id+"F2.wireOp",EDGE,"E1.top"),sQuery(id+"F2.wireOp",EDGE,"E1.left"),sQuery(id+"F2.wireOp",EDGE,"E1.right"),sQuery(id+"F2.wireOp",EDGE,"E2.top"),sQuery(id+"F2.wireOp",EDGE,"E2.left"),sQuery(id+"F2.wireOp",EDGE,"E2.right"),sQuery(id+"F2.wireOp",EDGE,"E4.bottom"),sQuery(id+"F2.wireOp",EDGE,"E4.top"),sQuery(id+"F2.wireOp",EDGE,"E4.left"),sQuery(id+"F2.wireOp",EDGE,"E4.right"),sQuery(id+"F2.wireOp",EDGE,"E5.filletArc"),sQuery(id+"F2.wireOp",EDGE,"E6.filletArc"),sQuery(id+"F2.wireOp",EDGE,"E7.filletArc"),sQuery(id+"F2.wireOp",EDGE,"E8.filletArc")])]});
            var Q1;
            Q1=makeQuery(id+"F9.opExtrude","CAP_EDGE",EDGE,{"disambiguationData":[OSD([sQuery(id+"F8.wireOp",EDGE,"E31")])],"isStart":true});
            transform(context, id + "F50", {"entities" : qUnion([Q0]), "transformType" : TransformType.TRANSLATION_ENTITY, "oppositeDirectionEntity" : false, "transformLine" : qUnion([Q1]), "makeCopy" : true});
        }
        {
            var Q0;
            Q0=makeQuery(id+"F50.opPattern","COPY",BODY,{"derivedFrom":makeQuery(id+"F3.opExtrude","SWEPT_BODY",BODY,{"disambiguationData":[OSD([sQuery(id+"F2.wireOp",EDGE,"E1.bottom"),sQuery(id+"F2.wireOp",EDGE,"E1.top"),sQuery(id+"F2.wireOp",EDGE,"E1.left"),sQuery(id+"F2.wireOp",EDGE,"E1.right"),sQuery(id+"F2.wireOp",EDGE,"E2.top"),sQuery(id+"F2.wireOp",EDGE,"E2.left"),sQuery(id+"F2.wireOp",EDGE,"E2.right"),sQuery(id+"F2.wireOp",EDGE,"E4.bottom"),sQuery(id+"F2.wireOp",EDGE,"E4.top"),sQuery(id+"F2.wireOp",EDGE,"E4.left"),sQuery(id+"F2.wireOp",EDGE,"E4.right"),sQuery(id+"F2.wireOp",EDGE,"E5.filletArc"),sQuery(id+"F2.wireOp",EDGE,"E6.filletArc"),sQuery(id+"F2.wireOp",EDGE,"E7.filletArc"),sQuery(id+"F2.wireOp",EDGE,"E8.filletArc")])]}),"instanceName":"1"});
            var Q1;
            Q1=makeQuery(id+"F1.opExtrude","CAP_EDGE",EDGE,{"disambiguationData":[OSD([sQuery(id+"F0.wireOp",EDGE,"E0.bottom")])],"isStart":false});
            transform(context, id + "F51", {"entities" : qUnion([Q0]), "transformType" : TransformType.TRANSLATION_DISTANCE, "transformDirection" : qUnion([Q1]), "distance" : 10 * mm, "oppositeDirection" : true, "makeCopy" : false});
        }
    });
